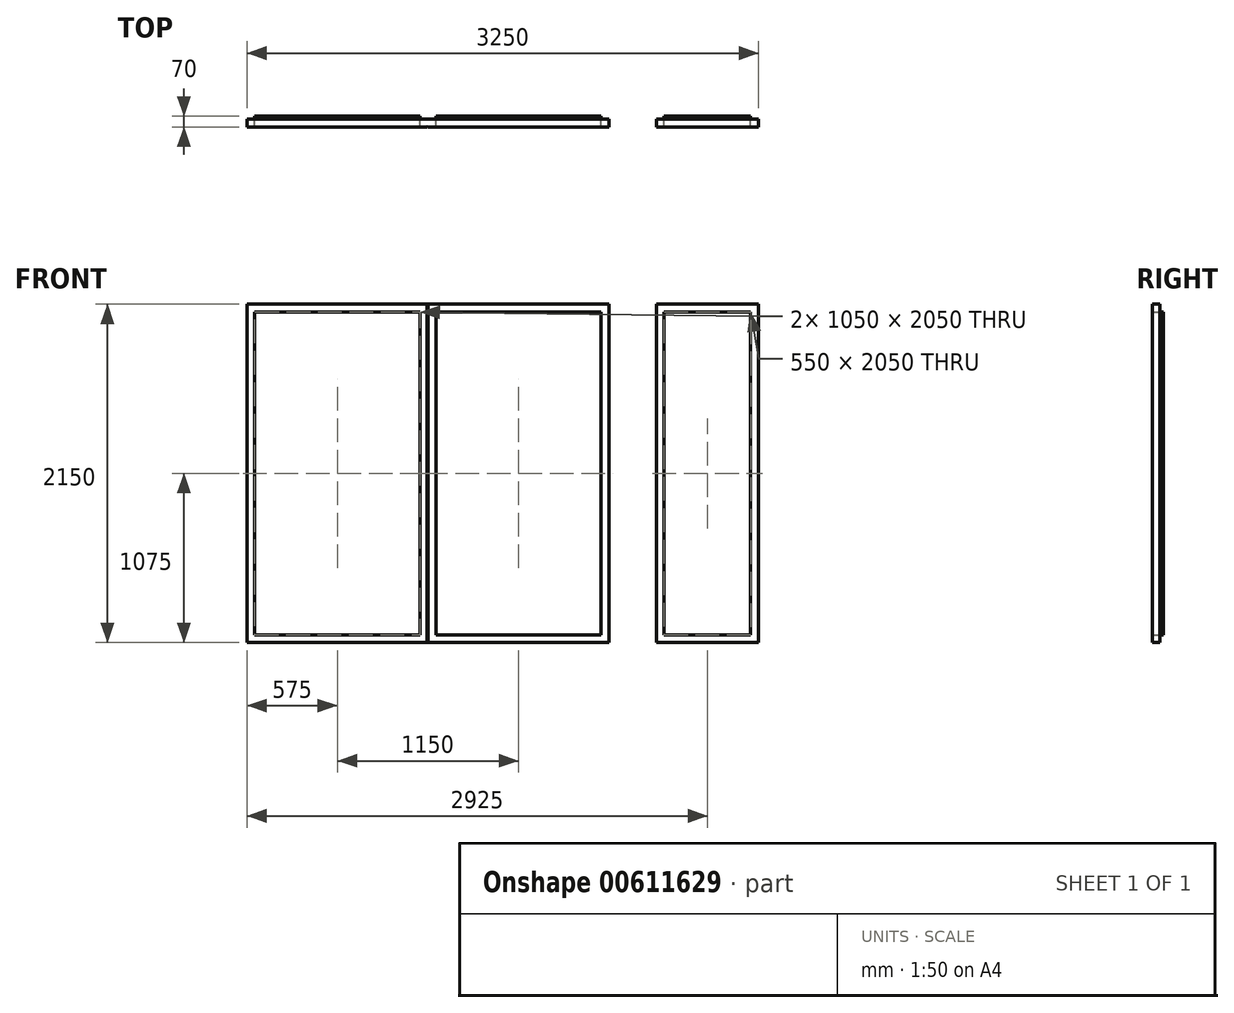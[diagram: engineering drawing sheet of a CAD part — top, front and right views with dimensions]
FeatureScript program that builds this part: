
annotation { "Feature Type Name" : "Feature", "Feature Type Description" : "" }
export const myFeature = defineFeature(function(context is Context, id is Id, definition is map)
    precondition{}
    {
        {
            var Q0;
            Q0=qCreatedBy(makeId("Front.planeOp"),FACE);
            var sketch = newSketch(context, id + "F0", { "sketchPlane" : qUnion([Q0])});
            skLineSegment(sketch, "E0.bottom", {"start": v(0, 0) * mm, "end": v(2300, 0) * mm});
            skLineSegment(sketch, "E0.top", {"start": v(0, 2150) * mm, "end": v(2300, 2150) * mm});
            skLineSegment(sketch, "E0.left", {"start": v(0, 0) * mm, "end": v(0, 2150) * mm});
            skLineSegment(sketch, "E0.right", {"start": v(2300, 0) * mm, "end": v(2300, 2150) * mm});
            skLineSegment(sketch, "E1.bottom", {"start": v(2600, 0) * mm, "end": v(3250, 0) * mm});
            skLineSegment(sketch, "E1.top", {"start": v(2600, 2150) * mm, "end": v(3250, 2150) * mm});
            skLineSegment(sketch, "E1.left", {"start": v(2600, 0) * mm, "end": v(2600, 2150) * mm});
            skLineSegment(sketch, "E1.right", {"start": v(3250, 0) * mm, "end": v(3250, 2150) * mm});
            skLineSegment(sketch, "E2", {"start": v(1150, 2150) * mm, "end": v(1150, 0) * mm});
            skLineSegment(sketch, "E3.bottom", {"start": v(50, 2100) * mm, "end": v(1100, 2100) * mm});
            skLineSegment(sketch, "E3.top", {"start": v(50, 50) * mm, "end": v(1100, 50) * mm});
            skLineSegment(sketch, "E3.left", {"start": v(50, 2100) * mm, "end": v(50, 50) * mm});
            skLineSegment(sketch, "E3.right", {"start": v(1100, 2100) * mm, "end": v(1100, 50) * mm});
            skLineSegment(sketch, "E4.bottom", {"start": v(1200, 2100) * mm, "end": v(2250, 2100) * mm});
            skLineSegment(sketch, "E4.top", {"start": v(1200, 50) * mm, "end": v(2250, 50) * mm});
            skLineSegment(sketch, "E4.left", {"start": v(1200, 2100) * mm, "end": v(1200, 50) * mm});
            skLineSegment(sketch, "E4.right", {"start": v(2250, 2100) * mm, "end": v(2250, 50) * mm});
            skLineSegment(sketch, "E5.bottom", {"start": v(2650, 2100) * mm, "end": v(3200, 2100) * mm});
            skLineSegment(sketch, "E5.top", {"start": v(2650, 50) * mm, "end": v(3200, 50) * mm});
            skLineSegment(sketch, "E5.left", {"start": v(2650, 2100) * mm, "end": v(2650, 50) * mm});
            skLineSegment(sketch, "E5.right", {"start": v(3200, 2100) * mm, "end": v(3200, 50) * mm});
            skSolve(sketch);
        }
        {
            var Q0;
            {var subQ0=sQuery(id+"F0.wireOp",EDGE,"E0.left");Q0=makeQuery(id+"F0.imprint","IMPRINT",FACE,{"disambiguationData":[TD([[makeQuery(id+"F0.imprint","IMPRINT",EDGE,{"derivedFrom":subQ0}),-1.0]])]});}
            extrude(context, id + "F1", {"entities" : qUnion([Q0]), "depth" : 50 * mm, "offsetDistance" : 25 * mm});
        }
        {
            var Q0;
            Q0=makeQuery(id+"F1.opExtrude","CAP_EDGE",EDGE,{"disambiguationData":[OSD([sQuery(id+"F0.wireOp",EDGE,"E2")])],"isStart":false});
            chamfer(context, id + "F2", {"entities" : qUnion([Q0]), "width" : 5 * mm, "tangentPropagation" : true});
        }
        {
            var Q0;
            {var subQ1=sQuery(id+"F0.wireOp",EDGE,"E0.right");Q0=makeQuery(id+"F0.imprint","IMPRINT",FACE,{"disambiguationData":[TD([[makeQuery(id+"F0.imprint","IMPRINT",EDGE,{"derivedFrom":subQ1}),1.0]])]});}
            extrude(context, id + "F3", {"entities" : qUnion([Q0]), "operationType" : NewBodyOperationType.ADD, "depth" : 50 * mm, "offsetDistance" : 25 * mm});
        }
        {
            var Q0;
            Q0=makeQuery(id+"F0.imprint","IMPRINT",FACE,{"disambiguationData":[TD([[makeQuery(id+"F0.imprint","IMPRINT",EDGE,{"derivedFrom":sQuery(id+"F0.wireOp",EDGE,"E1.bottom")}),1.0]])]});
            extrude(context, id + "F4", {"entities" : qUnion([Q0]), "depth" : 50 * mm, "offsetDistance" : 25 * mm});
        }
        {
            var Q0;
            Q0=makeQuery(id+"F0.imprint","IMPRINT",FACE,{"disambiguationData":[TD([[makeQuery(id+"F0.imprint","IMPRINT",EDGE,{"derivedFrom":sQuery(id+"F0.wireOp",EDGE,"E3.bottom")}),-1.0]])]});
            var Q1;
            Q1=makeQuery(id+"F0.imprint","IMPRINT",FACE,{"disambiguationData":[TD([[makeQuery(id+"F0.imprint","IMPRINT",EDGE,{"derivedFrom":sQuery(id+"F0.wireOp",EDGE,"E4.bottom")}),-1.0]])]});
            var Q2;
            Q2=makeQuery(id+"F0.imprint","IMPRINT",FACE,{"disambiguationData":[TD([[makeQuery(id+"F0.imprint","IMPRINT",EDGE,{"derivedFrom":sQuery(id+"F0.wireOp",EDGE,"E5.bottom")}),-1.0]])]});
            extrude(context, id + "F5", {"entities" : qUnion([Q0, Q1, Q2]), "oppositeDirection" : true, "depth" : 20 * mm, "offsetDistance" : 25 * mm});
        }
    });
